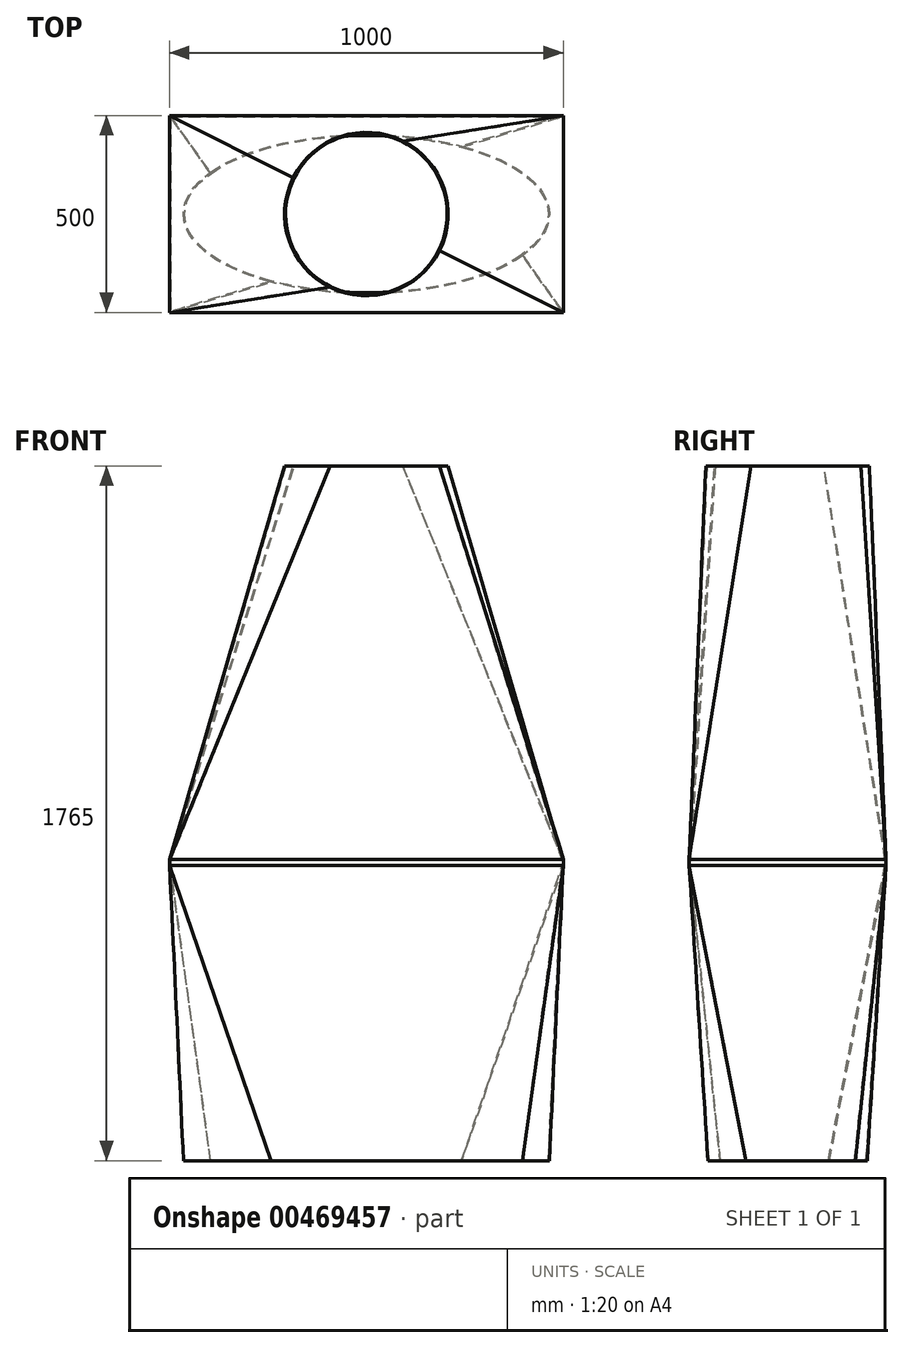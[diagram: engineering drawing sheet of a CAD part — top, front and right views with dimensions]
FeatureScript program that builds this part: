
annotation { "Feature Type Name" : "Feature", "Feature Type Description" : "" }
export const myFeature = defineFeature(function(context is Context, id is Id, definition is map)
    precondition{}
    {
        {
            var Q0;
            Q0=qCreatedBy(makeId("Top.planeOp"),FACE);
            var sketch = newSketch(context, id + "F0", { "sketchPlane" : qUnion([Q0])});
            skLineSegment(sketch, "E0.bottom", {"start": v(-500, 250) * mm, "end": v(500, 250) * mm});
            skLineSegment(sketch, "E0.top", {"start": v(-500, -250) * mm, "end": v(500, -250) * mm});
            skLineSegment(sketch, "E0.left", {"start": v(-500, 250) * mm, "end": v(-500, -250) * mm});
            skLineSegment(sketch, "E0.right", {"start": v(500, 250) * mm, "end": v(500, -250) * mm});
            skPoint(sketch, "E0.middle", {"position": v(0, 0) * mm});
            skSolve(sketch);
        }
        {
            var Q0;
            Q0=makeQuery(id+"F0.imprint","IMPRINT",FACE,{"disambiguationData":[TD([[makeQuery(id+"F0.imprint","IMPRINT",EDGE,{"derivedFrom":sQuery(id+"F0.wireOp",EDGE,"E0.bottom")}),-1.0]])]});
            extrude(context, id + "F1", {"entities" : qUnion([Q0]), "depth" : 15 * mm});
        }
        {
            var Q0;
            Q0=makeQuery(id+"F1.opExtrude","CAP_FACE",FACE,{"disambiguationData":[OSD([sQuery(id+"F0.wireOp",EDGE,"E0.bottom"),sQuery(id+"F0.wireOp",EDGE,"E0.top"),sQuery(id+"F0.wireOp",EDGE,"E0.left"),sQuery(id+"F0.wireOp",EDGE,"E0.right")])],"isStart":false});
            cPlane(context, id + "F2", {"entities" : qUnion([Q0]), "cplaneType" : CPlaneType.OFFSET, "offset" : 1000 * mm, "width" : 150 * mm, "height" : 150 * mm});
        }
        {
            var Q0;
            Q0=qCreatedBy(id+"F2.planeOp",FACE);
            var sketch = newSketch(context, id + "F3", { "sketchPlane" : qUnion([Q0])});
            skCircle(sketch, "E1", {"center": v(0, 0) * mm, "radius": 207.83 * mm});
            skSolve(sketch);
        }
        {
            var Q1;
            Q1=makeQuery(id+"F1.opExtrude","CAP_FACE",FACE,{"disambiguationData":[OSD([sQuery(id+"F0.wireOp",EDGE,"E0.bottom"),sQuery(id+"F0.wireOp",EDGE,"E0.top"),sQuery(id+"F0.wireOp",EDGE,"E0.left"),sQuery(id+"F0.wireOp",EDGE,"E0.right")])],"isStart":false});
            var Q2;
            Q2=makeQuery(id+"F3.imprint","IMPRINT",FACE,{"disambiguationData":[TD([[makeQuery(id+"F3.imprint","IMPRINT",EDGE,{"derivedFrom":sQuery(id+"F3.wireOp",EDGE,"E1")}),1.0]])]});
            loft(context, id + "F4", {"operationType" : NewBodyOperationType.ADD, "sheetProfilesArray" : [{ "sheetProfileEntities" : qUnion([Q1]) }, { "sheetProfileEntities" : qUnion([Q2]) }]});
        }
        {
            var Q0;
            Q0=makeQuery(id+"F1.opExtrude","CAP_FACE",FACE,{"disambiguationData":[OSD([sQuery(id+"F0.wireOp",EDGE,"E0.bottom"),sQuery(id+"F0.wireOp",EDGE,"E0.top"),sQuery(id+"F0.wireOp",EDGE,"E0.left"),sQuery(id+"F0.wireOp",EDGE,"E0.right")])],"isStart":true});
            cPlane(context, id + "F5", {"entities" : qUnion([Q0]), "cplaneType" : CPlaneType.OFFSET, "offset" : 750 * mm, "width" : 150 * mm, "height" : 150 * mm});
        }
        {
            var Q0;
            Q0=qCreatedBy(id+"F5.planeOp",FACE);
            var sketch = newSketch(context, id + "F6", { "sketchPlane" : qUnion([Q0])});
            skEllipse(sketch, "E2", {"center": v(0, 0) * mm, "majorRadius": 464.83 * mm, "minorRadius": 202.19 * mm, "majorAxis": v(1, 0)});
            skSolve(sketch);
        }
        {
            var Q0;
            Q0=makeQuery(id+"F1.opExtrude","CAP_FACE",FACE,{"disambiguationData":[OSD([sQuery(id+"F0.wireOp",EDGE,"E0.bottom"),sQuery(id+"F0.wireOp",EDGE,"E0.top"),sQuery(id+"F0.wireOp",EDGE,"E0.left"),sQuery(id+"F0.wireOp",EDGE,"E0.right")])],"isStart":true});
            var sketch = newSketch(context, id + "F7", { "sketchPlane" : qUnion([Q0])});
            skLineSegment(sketch, "E3.bottom", {"start": v(-500, 250) * mm, "end": v(500, 250) * mm});
            skLineSegment(sketch, "E3.top", {"start": v(-500, -250) * mm, "end": v(500, -250) * mm});
            skLineSegment(sketch, "E3.left", {"start": v(-500, 250) * mm, "end": v(-500, -250) * mm});
            skLineSegment(sketch, "E3.right", {"start": v(500, 250) * mm, "end": v(500, -250) * mm});
            skSolve(sketch);
        }
        {
            var Q1;
            Q1 = qSketchRegion(id + "F7", true);
            var Q2;
            Q2 = qSketchRegion(id + "F6", true);
            loft(context, id + "F8", {"operationType" : NewBodyOperationType.ADD, "sheetProfilesArray" : [{ "sheetProfileEntities" : qUnion([Q1]) }, { "sheetProfileEntities" : qUnion([Q2]) }]});
        }
        {
            var Q0;
            Q0=makeQuery(id+"F4.opLoft","CAP_FACE",FACE,{"disambiguationData":[OSD([makeQuery(id+"F3.imprint","IMPRINT",FACE,{"disambiguationData":[TD([[makeQuery(id+"F3.imprint","IMPRINT",EDGE,{"derivedFrom":sQuery(id+"F3.wireOp",EDGE,"E1")}),1.0]])]})])],"isStart":true});
            var Q1;
            Q1=makeQuery(id+"F8.opLoft","CAP_FACE",FACE,{"disambiguationData":[OSD([makeQuery(id+"F6.imprint","IMPRINT",FACE,{"disambiguationData":[TD([[makeQuery(id+"F6.imprint","IMPRINT",EDGE,{"derivedFrom":sQuery(id+"F6.wireOp",EDGE,"E2")}),1.0]])]})])],"isStart":true});
            shell(context, id + "F9", {"entities" : qUnion([Q0, Q1]), "thickness" : 2.5 * mm});
        }
    });
